# Revit family: Sink-Undermount-Acorn-SU-1916-80
name_source: partatom
category: Plumbing Fixtures
units: mm (PartAtom-declared; Revit-internal decimal feet)

## family parameters
Cut with Voids When Loaded = No
Host = Face
OmniClass Number = 23.45.05.14.14
OmniClass Title = Sinks/Lavatories
Part Type = Normal
Room Calculation Point = No
Round Connector Dimension = Use Diameter
Shared = Yes

## types (1)
- SU-1916-80
    -80 8” Deep Bowl = Yes
    Assembly Code = D2010440
    CW Connection = No
    CWFU = 3
    Compliance Certifications = ASME A112.19.3/CSA B45.4, IAPMO® Certified for Conformance with Uniform Plumbing Code (UPC ), International Plumbing Code (IPC ), National Plumbing Code of Canada (NPC )
    Countertop Thickness = 1/2"
    Default Elevation = 34"
    Description = Acorn-Sinks® Stainless Steel Undermount Sink, 19" x 16"
    Drain Size = 3 1/2"
    Finish = Stainless Steel-18 Gauge-Type 304-Acorn-Satin
    HW Connection = No
    HWFU = 3
    Installation Type = Undermount
    Length = 18 1/2"
    Manufacturer = Acorn
    Model = SU-1916-80
    Product Documentation Link = https://www.acorneng.com
    Product Page URL = https://www.acorneng.com
    Sink Bowl Depth = 8"
    Sink Bowl Length = 16"
    Sink Bowl Width = 19"
    URL = https://www.acorneng.com
    Vent Connection = No
    WFU = 4
    Waste Connection = No
    Width = 21 1/2"
    cUPC Compliant = Yes

## geometry (parser evidence)
native form markers: Sweep x3
no freeform markers — native parametric forms only
